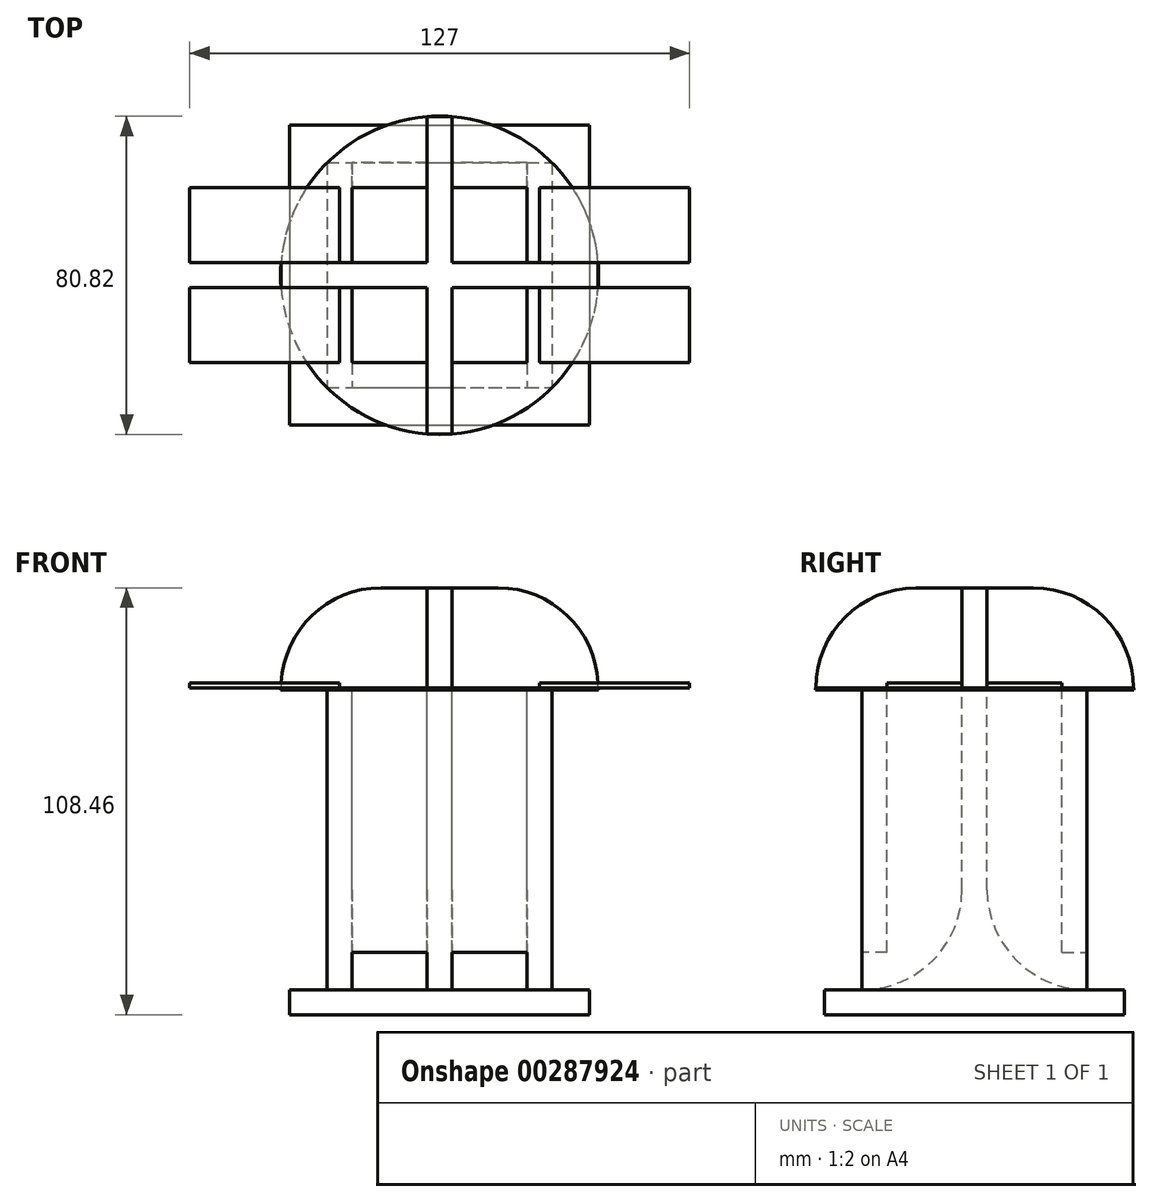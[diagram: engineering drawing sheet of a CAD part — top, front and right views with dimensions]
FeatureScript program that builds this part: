
annotation { "Feature Type Name" : "Feature", "Feature Type Description" : "" }
export const myFeature = defineFeature(function(context is Context, id is Id, definition is map)
    precondition{}
    {
        {
            var Q0;
            Q0=qCreatedBy(makeId("Top.planeOp"),FACE);
            var sketch = newSketch(context, id + "F0", { "sketchPlane" : qUnion([Q0])});
            skLineSegment(sketch, "E0.bottom", {"start": v(-79.3, 58.47) * mm, "end": v(-3.1, 58.47) * mm});
            skLineSegment(sketch, "E0.top", {"start": v(-79.3, -17.73) * mm, "end": v(-3.1, -17.73) * mm});
            skLineSegment(sketch, "E0.left", {"start": v(-79.3, 58.47) * mm, "end": v(-79.3, -17.73) * mm});
            skLineSegment(sketch, "E0.right", {"start": v(-3.1, 58.47) * mm, "end": v(-3.1, -17.73) * mm});
            skSolve(sketch);
        }
        {
            var Q0;
            Q0=makeQuery(id+"F0.imprint","IMPRINT",FACE,{"disambiguationData":[TD([[makeQuery(id+"F0.imprint","IMPRINT",EDGE,{"derivedFrom":sQuery(id+"F0.wireOp",EDGE,"E0.bottom")}),-1.0]])]});
            extrude(context, id + "F1", {"entities" : qUnion([Q0]), "depth" : 6.35 * mm, "offsetDistance" : 25.4 * mm});
        }
        {
            var Q0;
            Q0=makeQuery(id+"F1.opExtrude","CAP_FACE",FACE,{"disambiguationData":[OSD([sQuery(id+"F0.wireOp",EDGE,"E0.bottom"),sQuery(id+"F0.wireOp",EDGE,"E0.top"),sQuery(id+"F0.wireOp",EDGE,"E0.left"),sQuery(id+"F0.wireOp",EDGE,"E0.right")])],"isStart":false});
            var sketch = newSketch(context, id + "F2", { "sketchPlane" : qUnion([Q0])});
            skLineSegment(sketch, "E1.bottom", {"start": v(-69.78, 48.95) * mm, "end": v(-12.63, 48.95) * mm});
            skLineSegment(sketch, "E1.top", {"start": v(-69.78, -8.2) * mm, "end": v(-12.63, -8.2) * mm});
            skLineSegment(sketch, "E1.left", {"start": v(-69.78, 48.95) * mm, "end": v(-69.78, -8.2) * mm});
            skLineSegment(sketch, "E1.right", {"start": v(-12.63, 48.95) * mm, "end": v(-12.63, -8.2) * mm});
            skSolve(sketch);
        }
        {
            var Q0;
            Q0=makeQuery(id+"F2.imprint","IMPRINT",FACE,{"disambiguationData":[TD([[makeQuery(id+"F2.imprint","IMPRINT",EDGE,{"derivedFrom":sQuery(id+"F2.wireOp",EDGE,"E1.bottom")}),-1.0]])]});
            extrude(context, id + "F3", {"entities" : qUnion([Q0]), "operationType" : NewBodyOperationType.ADD, "depth" : 76.2 * mm, "offsetDistance" : 25.4 * mm});
        }
        {
            var Q0;
            Q0=makeQuery(id+"F3.opExtrude","CAP_FACE",FACE,{"disambiguationData":[OSD([sQuery(id+"F2.wireOp",EDGE,"E1.bottom"),sQuery(id+"F2.wireOp",EDGE,"E1.top"),sQuery(id+"F2.wireOp",EDGE,"E1.left"),sQuery(id+"F2.wireOp",EDGE,"E1.right")])],"isStart":false});
            var sketch = newSketch(context, id + "F4", { "sketchPlane" : qUnion([Q0])});
            skLineSegment(sketch, "E2.bottom", {"start": v(-63.43, 42.6) * mm, "end": v(-44.38, 42.6) * mm});
            skLineSegment(sketch, "E2.top", {"start": v(-63.43, 23.55) * mm, "end": v(-44.38, 23.55) * mm});
            skLineSegment(sketch, "E2.left", {"start": v(-63.43, 42.6) * mm, "end": v(-63.43, 23.55) * mm});
            skLineSegment(sketch, "E2.right", {"start": v(-44.38, 42.6) * mm, "end": v(-44.38, 23.55) * mm});
            skLineSegment(sketch, "E3.bottom", {"start": v(-38.03, 42.6) * mm, "end": v(-18.98, 42.6) * mm});
            skLineSegment(sketch, "E3.top", {"start": v(-38.03, 23.55) * mm, "end": v(-18.98, 23.55) * mm});
            skLineSegment(sketch, "E3.left", {"start": v(-38.03, 42.6) * mm, "end": v(-38.03, 23.55) * mm});
            skLineSegment(sketch, "E3.right", {"start": v(-18.98, 42.6) * mm, "end": v(-18.98, 23.55) * mm});
            skLineSegment(sketch, "E4.bottom", {"start": v(-38.03, 17.2) * mm, "end": v(-18.98, 17.2) * mm});
            skLineSegment(sketch, "E4.top", {"start": v(-38.03, -1.85) * mm, "end": v(-18.98, -1.85) * mm});
            skLineSegment(sketch, "E4.left", {"start": v(-38.03, 17.2) * mm, "end": v(-38.03, -1.85) * mm});
            skLineSegment(sketch, "E4.right", {"start": v(-18.98, 17.2) * mm, "end": v(-18.98, -1.85) * mm});
            skLineSegment(sketch, "E5.bottom", {"start": v(-63.43, 17.2) * mm, "end": v(-44.38, 17.2) * mm});
            skLineSegment(sketch, "E5.top", {"start": v(-63.43, -1.85) * mm, "end": v(-44.38, -1.85) * mm});
            skLineSegment(sketch, "E5.left", {"start": v(-63.43, 17.2) * mm, "end": v(-63.43, -1.85) * mm});
            skLineSegment(sketch, "E5.right", {"start": v(-44.38, 17.2) * mm, "end": v(-44.38, -1.85) * mm});
            skSolve(sketch);
        }
        {
            var Q0;
            Q0=makeQuery(id+"F4.imprint","IMPRINT",FACE,{"disambiguationData":[TD([[makeQuery(id+"F4.imprint","IMPRINT",EDGE,{"derivedFrom":sQuery(id+"F4.wireOp",EDGE,"E2.bottom")}),-1.0]])]});
            var Q1;
            Q1=makeQuery(id+"F4.imprint","IMPRINT",FACE,{"disambiguationData":[TD([[makeQuery(id+"F4.imprint","IMPRINT",EDGE,{"derivedFrom":sQuery(id+"F4.wireOp",EDGE,"E3.bottom")}),-1.0]])]});
            var Q2;
            Q2=makeQuery(id+"F4.imprint","IMPRINT",FACE,{"disambiguationData":[TD([[makeQuery(id+"F4.imprint","IMPRINT",EDGE,{"derivedFrom":sQuery(id+"F4.wireOp",EDGE,"E4.bottom")}),-1.0]])]});
            var Q3;
            Q3=makeQuery(id+"F4.imprint","IMPRINT",FACE,{"disambiguationData":[TD([[makeQuery(id+"F4.imprint","IMPRINT",EDGE,{"derivedFrom":sQuery(id+"F4.wireOp",EDGE,"E5.bottom")}),-1.0]])]});
            extrude(context, id + "F5", {"entities" : qUnion([Q0, Q1, Q2, Q3]), "operationType" : NewBodyOperationType.REMOVE, "oppositeDirection" : true, "depth" : 76.2 * mm, "offsetDistance" : 25.4 * mm, "hasSecondDirection" : true, "secondDirectionOppositeDirection" : false, "secondDirectionDepth" : 25.4 * mm});
        }
        {
            var Q0;
            Q0=makeQuery(id+"F3.opExtrude","SWEPT_FACE",FACE,{"disambiguationData":[OSD([sQuery(id+"F2.wireOp",EDGE,"E1.top")])]});
            var sketch = newSketch(context, id + "F6", { "sketchPlane" : qUnion([Q0])});
            skLineSegment(sketch, "E6.bottom", {"start": v(-63.43, 15.88) * mm, "end": v(-18.98, 15.88) * mm});
            skLineSegment(sketch, "E6.top", {"start": v(-63.43, 6.35) * mm, "end": v(-18.98, 6.35) * mm});
            skLineSegment(sketch, "E6.left", {"start": v(-63.43, 15.88) * mm, "end": v(-63.43, 6.35) * mm});
            skLineSegment(sketch, "E6.right", {"start": v(-18.98, 15.88) * mm, "end": v(-18.98, 6.35) * mm});
            skLineSegment(sketch, "E7", {"start": v(-44.38, 15.87) * mm, "end": v(-44.38, 6.35) * mm});
            skLineSegment(sketch, "E8", {"start": v(-38.03, 6.35) * mm, "end": v(-38.03, 15.87) * mm});
            skSolve(sketch);
        }
        {
            var Q0;
            Q0=makeQuery(id+"F3.opExtrude","SWEPT_FACE",FACE,{"disambiguationData":[OSD([sQuery(id+"F2.wireOp",EDGE,"E1.bottom")])]});
            var sketch = newSketch(context, id + "F7", { "sketchPlane" : qUnion([Q0])});
            skLineSegment(sketch, "E9.bottom", {"start": v(18.98, 6.35) * mm, "end": v(63.43, 6.35) * mm});
            skLineSegment(sketch, "E9.top", {"start": v(18.98, 15.88) * mm, "end": v(63.43, 15.88) * mm});
            skLineSegment(sketch, "E9.left", {"start": v(18.98, 6.35) * mm, "end": v(18.98, 15.88) * mm});
            skLineSegment(sketch, "E9.right", {"start": v(63.43, 6.35) * mm, "end": v(63.43, 15.88) * mm});
            skLineSegment(sketch, "E10", {"start": v(38.03, 15.88) * mm, "end": v(38.03, 6.35) * mm});
            skLineSegment(sketch, "E11", {"start": v(44.38, 15.88) * mm, "end": v(44.38, 6.35) * mm});
            skSolve(sketch);
        }
        {
            var Q0;
            {var subQ0=sQuery(id+"F7.wireOp",EDGE,"E9.left");Q0=makeQuery(id+"F7.imprint","IMPRINT",FACE,{"disambiguationData":[TD([[makeQuery(id+"F7.imprint","IMPRINT",EDGE,{"derivedFrom":subQ0}),-1.0]])]});}
            var Q1;
            {var subQ0=sQuery(id+"F7.wireOp",EDGE,"E9.right");Q1=makeQuery(id+"F7.imprint","IMPRINT",FACE,{"disambiguationData":[TD([[makeQuery(id+"F7.imprint","IMPRINT",EDGE,{"derivedFrom":subQ0}),1.0]])]});}
            var Q2;
            {var subQ0=sQuery(id+"F6.wireOp",EDGE,"E6.right");Q2=makeQuery(id+"F6.imprint","IMPRINT",FACE,{"disambiguationData":[TD([[makeQuery(id+"F6.imprint","IMPRINT",EDGE,{"derivedFrom":subQ0}),-1.0]])]});}
            var Q3;
            {var subQ0=sQuery(id+"F6.wireOp",EDGE,"E6.left");Q3=makeQuery(id+"F6.imprint","IMPRINT",FACE,{"disambiguationData":[TD([[makeQuery(id+"F6.imprint","IMPRINT",EDGE,{"derivedFrom":subQ0}),1.0]])]});}
            extrude(context, id + "F8", {"entities" : qUnion([Q0, Q1, Q2, Q3]), "operationType" : NewBodyOperationType.REMOVE, "oppositeDirection" : true, "depth" : 6.35 * mm, "offsetDistance" : 25.4 * mm});
        }
        {
            var Q0;
            {var subQ0=sQuery(id+"F6.wireOp",EDGE,"E6.left");Q0=makeQuery(id+"F6.imprint","IMPRINT",FACE,{"disambiguationData":[TD([[makeQuery(id+"F6.imprint","IMPRINT",EDGE,{"derivedFrom":subQ0}),1.0]])]});}
            var Q1;
            {var subQ0=sQuery(id+"F6.wireOp",EDGE,"E6.right");Q1=makeQuery(id+"F6.imprint","IMPRINT",FACE,{"disambiguationData":[TD([[makeQuery(id+"F6.imprint","IMPRINT",EDGE,{"derivedFrom":subQ0}),-1.0]])]});}
            extrude(context, id + "F9", {"entities" : qUnion([Q0, Q1]), "operationType" : NewBodyOperationType.REMOVE, "oppositeDirection" : true, "depth" : 6.35 * mm, "offsetDistance" : 25.4 * mm});
        }
        {
            var Q0;
            Q0=makeQuery(id+"F5.boolean.opBoolean","COPY",EDGE,{"derivedFrom":makeQuery(id+"F5.opExtrude","CAP_EDGE",EDGE,{"disambiguationData":[OSD([sQuery(id+"F4.wireOp",EDGE,"E5.bottom")])],"isStart":false})});
            var Q1;
            Q1=makeQuery(id+"F5.boolean.opBoolean","COPY",EDGE,{"derivedFrom":makeQuery(id+"F5.opExtrude","CAP_EDGE",EDGE,{"disambiguationData":[OSD([sQuery(id+"F4.wireOp",EDGE,"E4.bottom")])],"isStart":false})});
            var Q2;
            Q2=makeQuery(id+"F5.boolean.opBoolean","COPY",EDGE,{"derivedFrom":makeQuery(id+"F5.opExtrude","CAP_EDGE",EDGE,{"disambiguationData":[OSD([sQuery(id+"F4.wireOp",EDGE,"E2.top")])],"isStart":false})});
            var Q3;
            Q3=makeQuery(id+"F5.boolean.opBoolean","COPY",EDGE,{"derivedFrom":makeQuery(id+"F5.opExtrude","CAP_EDGE",EDGE,{"disambiguationData":[OSD([sQuery(id+"F4.wireOp",EDGE,"E3.top")])],"isStart":false})});
            fillet(context, id + "F10", {"entities" : qUnion([Q0, Q1, Q2, Q3]), "radius" : 25.4 * mm, "tangentPropagation" : true, "allowEdgeOverflow" : false});
        }
        {
            var Q0;
            Q0=makeQuery(id+"F3.opExtrude","CAP_FACE",FACE,{"disambiguationData":[OSD([sQuery(id+"F2.wireOp",EDGE,"E1.bottom"),sQuery(id+"F2.wireOp",EDGE,"E1.top"),sQuery(id+"F2.wireOp",EDGE,"E1.left"),sQuery(id+"F2.wireOp",EDGE,"E1.right")])],"isStart":false});
            var sketch = newSketch(context, id + "F11", { "sketchPlane" : qUnion([Q0])});
            skCircle(sketch, "E12", {"center": v(-41.2, 20.37) * mm, "radius": 40.41 * mm});
            skLineSegment(sketch, "E13", {"start": v(-41.2, 71.25) * mm, "end": v(-41.2, -44.9) * mm, "construction": true});
            skLineSegment(sketch, "E14", {"start": v(-126.27, 20.37) * mm, "end": v(52, 20.37) * mm, "construction": true});
            skLineSegment(sketch, "E15", {"start": v(-41.2, 60.78) * mm, "end": v(-41.2, -20.04) * mm});
            skSolve(sketch);
        }
        {
            var Q0;
            Q0 = qSketchRegion(id + "F11", true);
            extrude(context, id + "F12", {"entities" : qUnion([Q0]), "operationType" : NewBodyOperationType.ADD, "depth" : 0.5 * mm, "offsetDistance" : 25.4 * mm});
        }
        {
            var Q0;
            Q0 = qSketchRegion(id + "F4", true);
            extrude(context, id + "F13", {"entities" : qUnion([Q0]), "operationType" : NewBodyOperationType.REMOVE, "depth" : 25.4 * mm, "offsetDistance" : 25.4 * mm});
        }
        {
            var Q0;
            Q0=makeQuery(id+"F12.opExtrude","CAP_FACE",FACE,{"disambiguationData":[OSD([sQuery(id+"F11.wireOp",EDGE,"E12")])],"isStart":false});
            var sketch = newSketch(context, id + "F14", { "sketchPlane" : qUnion([Q0])});
            skLineSegment(sketch, "E16.bottom", {"start": v(-15.8, 23.55) * mm, "end": v(22.3, 23.55) * mm});
            skLineSegment(sketch, "E16.top", {"start": v(-15.8, 42.6) * mm, "end": v(22.3, 42.6) * mm});
            skLineSegment(sketch, "E16.left", {"start": v(-15.8, 23.55) * mm, "end": v(-15.8, 42.6) * mm});
            skLineSegment(sketch, "E16.right", {"start": v(22.3, 23.55) * mm, "end": v(22.3, 42.6) * mm});
            skLineSegment(sketch, "E17.bottom", {"start": v(-15.8, -1.85) * mm, "end": v(22.3, -1.85) * mm});
            skLineSegment(sketch, "E17.top", {"start": v(-15.8, 17.2) * mm, "end": v(22.3, 17.2) * mm});
            skLineSegment(sketch, "E17.left", {"start": v(-15.8, -1.85) * mm, "end": v(-15.8, 17.2) * mm});
            skLineSegment(sketch, "E17.right", {"start": v(22.3, -1.85) * mm, "end": v(22.3, 17.2) * mm});
            skLineSegment(sketch, "E18.bottom", {"start": v(-66.6, -1.85) * mm, "end": v(-104.7, -1.85) * mm});
            skLineSegment(sketch, "E18.top", {"start": v(-66.6, 17.2) * mm, "end": v(-104.7, 17.2) * mm});
            skLineSegment(sketch, "E18.left", {"start": v(-66.6, -1.85) * mm, "end": v(-66.6, 17.2) * mm});
            skLineSegment(sketch, "E18.right", {"start": v(-104.7, -1.85) * mm, "end": v(-104.7, 17.2) * mm});
            skLineSegment(sketch, "E19.bottom", {"start": v(-66.6, 23.55) * mm, "end": v(-104.7, 23.55) * mm});
            skLineSegment(sketch, "E19.top", {"start": v(-66.6, 42.6) * mm, "end": v(-104.7, 42.6) * mm});
            skLineSegment(sketch, "E19.left", {"start": v(-66.6, 23.55) * mm, "end": v(-66.6, 42.6) * mm});
            skLineSegment(sketch, "E19.right", {"start": v(-104.7, 23.55) * mm, "end": v(-104.7, 42.6) * mm});
            skSolve(sketch);
        }
        {
            var Q0;
            {var subQ0=sQuery(id+"F14.wireOp",EDGE,"E19.right");Q0=makeQuery(id+"F14.imprint","IMPRINT",FACE,{"disambiguationData":[TD([[makeQuery(id+"F14.imprint","IMPRINT",EDGE,{"derivedFrom":subQ0}),-1.0]])]});}
            var Q1;
            {var subQ0=sQuery(id+"F14.wireOp",EDGE,"E18.right");Q1=makeQuery(id+"F14.imprint","IMPRINT",FACE,{"disambiguationData":[TD([[makeQuery(id+"F14.imprint","IMPRINT",EDGE,{"derivedFrom":subQ0}),-1.0]])]});}
            var Q2;
            {var subQ0=sQuery(id+"F14.wireOp",EDGE,"E19.left");Q2=makeQuery(id+"F14.imprint","IMPRINT",FACE,{"disambiguationData":[TD([[makeQuery(id+"F14.imprint","IMPRINT",EDGE,{"derivedFrom":subQ0}),1.0]])]});}
            var Q3;
            {var subQ0=sQuery(id+"F14.wireOp",EDGE,"E18.left");Q3=makeQuery(id+"F14.imprint","IMPRINT",FACE,{"disambiguationData":[TD([[makeQuery(id+"F14.imprint","IMPRINT",EDGE,{"derivedFrom":subQ0}),1.0]])]});}
            var Q4;
            {var subQ0=sQuery(id+"F14.wireOp",EDGE,"E16.left");Q4=makeQuery(id+"F14.imprint","IMPRINT",FACE,{"disambiguationData":[TD([[makeQuery(id+"F14.imprint","IMPRINT",EDGE,{"derivedFrom":subQ0}),-1.0]])]});}
            var Q5;
            {var subQ0=sQuery(id+"F14.wireOp",EDGE,"E17.left");Q5=makeQuery(id+"F14.imprint","IMPRINT",FACE,{"disambiguationData":[TD([[makeQuery(id+"F14.imprint","IMPRINT",EDGE,{"derivedFrom":subQ0}),-1.0]])]});}
            var Q6;
            {var subQ0=sQuery(id+"F14.wireOp",EDGE,"E16.right");Q6=makeQuery(id+"F14.imprint","IMPRINT",FACE,{"disambiguationData":[TD([[makeQuery(id+"F14.imprint","IMPRINT",EDGE,{"derivedFrom":subQ0}),1.0]])]});}
            var Q7;
            {var subQ0=sQuery(id+"F14.wireOp",EDGE,"E17.right");Q7=makeQuery(id+"F14.imprint","IMPRINT",FACE,{"disambiguationData":[TD([[makeQuery(id+"F14.imprint","IMPRINT",EDGE,{"derivedFrom":subQ0}),1.0]])]});}
            extrude(context, id + "F15", {"entities" : qUnion([Q0, Q1, Q2, Q3, Q4, Q5, Q6, Q7]), "operationType" : NewBodyOperationType.ADD, "depth" : 1.27 * mm, "offsetDistance" : 25.4 * mm});
        }
        {
            var Q0;
            Q0=makeQuery(id+"F12.opExtrude","CAP_FACE",FACE,{"disambiguationData":[OSD([sQuery(id+"F11.wireOp",EDGE,"E12")])],"isStart":false});
            var sketch = newSketch(context, id + "F16", { "sketchPlane" : qUnion([Q0])});
            skLineSegment(sketch, "E20.bottom", {"start": v(-81.49, 17.2) * mm, "end": v(-0.92, 17.2) * mm});
            skLineSegment(sketch, "E20.top", {"start": v(-81.49, 23.55) * mm, "end": v(-0.92, 23.55) * mm});
            skLineSegment(sketch, "E20.left", {"start": v(-81.49, 17.2) * mm, "end": v(-81.49, 23.55) * mm});
            skLineSegment(sketch, "E20.right", {"start": v(-0.92, 17.2) * mm, "end": v(-0.92, 23.55) * mm});
            skLineSegment(sketch, "E21.bottom", {"start": v(-44.38, 60.66) * mm, "end": v(-38.03, 60.66) * mm});
            skLineSegment(sketch, "E21.top", {"start": v(-44.38, -19.92) * mm, "end": v(-38.03, -19.92) * mm});
            skLineSegment(sketch, "E21.left", {"start": v(-44.38, 60.66) * mm, "end": v(-44.38, -19.92) * mm});
            skLineSegment(sketch, "E21.right", {"start": v(-38.03, 60.66) * mm, "end": v(-38.03, -19.92) * mm});
            skSolve(sketch);
        }
        {
            var Q0;
            {var subQ4=sQuery(id+"F16.wireOp",EDGE,"E21.bottom");Q0=makeQuery(id+"F16.imprint","IMPRINT",FACE,{"disambiguationData":[TD([[makeQuery(id+"F16.imprint","IMPRINT",EDGE,{"derivedFrom":subQ4}),-1.0]])]});}
            var Q1;
            {var subQ9=sQuery(id+"F16.wireOp",EDGE,"E20.left");Q1=makeQuery(id+"F16.imprint","IMPRINT",FACE,{"disambiguationData":[TD([[makeQuery(id+"F16.imprint","IMPRINT",EDGE,{"derivedFrom":subQ9}),-1.0]])]});}
            var Q2;
            {var subQ9=sQuery(id+"F16.wireOp",EDGE,"E20.right");Q2=makeQuery(id+"F16.imprint","IMPRINT",FACE,{"disambiguationData":[TD([[makeQuery(id+"F16.imprint","IMPRINT",EDGE,{"derivedFrom":subQ9}),1.0]])]});}
            var Q3;
            {var subQ4=sQuery(id+"F16.wireOp",EDGE,"E21.top");Q3=makeQuery(id+"F16.imprint","IMPRINT",FACE,{"disambiguationData":[TD([[makeQuery(id+"F16.imprint","IMPRINT",EDGE,{"derivedFrom":subQ4}),1.0]])]});}
            var Q4;
            {var subQ0=sQuery(id+"F16.wireOp",EDGE,"E21.right");var subQ1=sQuery(id+"F16.wireOp",EDGE,"E20.bottom");var subQ2=makeQuery(id+"F16.imprint","INTERSECT",VERTEX,{"derivedFrom":[subQ1,subQ0]});var subQ3=sQuery(id+"F16.wireOp",EDGE,"E21.left");var subQ4=makeQuery(id+"F16.imprint","INTERSECT",VERTEX,{"derivedFrom":[subQ1,subQ3]});Q4=makeQuery(id+"F16.imprint","IMPRINT",FACE,{"disambiguationData":[TD([[makeQuery(id+"F16.imprint","IMPRINT",EDGE,{"disambiguationData":[TD([[subQ2,1.0],[subQ4,-1.0]])],"derivedFrom":subQ1}),1.0]])]});}
            extrude(context, id + "F17", {"entities" : qUnion([Q0, Q1, Q2, Q3, Q4]), "operationType" : NewBodyOperationType.ADD, "depth" : 25.4 * mm, "offsetDistance" : 25.4 * mm});
        }
        {
            var Q0;
            Q0=makeQuery(id+"F17.opExtrude","CAP_EDGE",EDGE,{"disambiguationData":[OSD([sQuery(id+"F16.wireOp",EDGE,"E21.top")])],"isStart":false});
            var Q1;
            Q1=makeQuery(id+"F17.opExtrude","CAP_EDGE",EDGE,{"disambiguationData":[OSD([sQuery(id+"F16.wireOp",EDGE,"E20.right")])],"isStart":false});
            var Q2;
            Q2=makeQuery(id+"F17.opExtrude","CAP_EDGE",EDGE,{"disambiguationData":[OSD([sQuery(id+"F16.wireOp",EDGE,"E21.bottom")])],"isStart":false});
            var Q3;
            Q3=makeQuery(id+"F17.opExtrude","CAP_EDGE",EDGE,{"disambiguationData":[OSD([sQuery(id+"F16.wireOp",EDGE,"E20.left")])],"isStart":false});
            fillet(context, id + "F18", {"entities" : qUnion([Q0, Q1, Q2, Q3]), "radius" : 25.4 * mm, "tangentPropagation" : true, "allowEdgeOverflow" : false});
        }
    });
